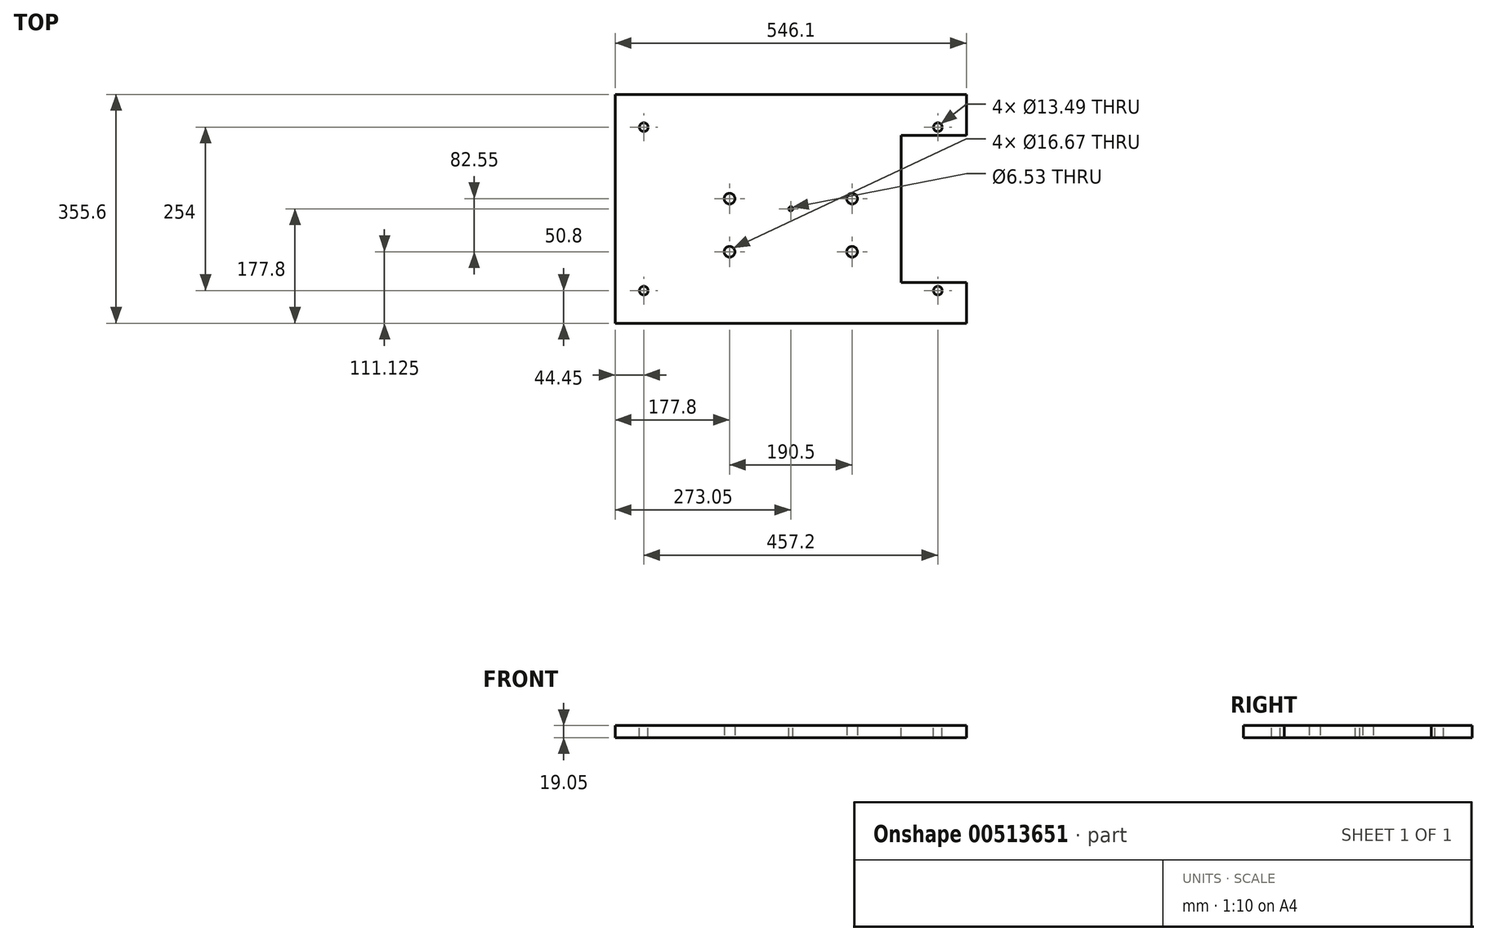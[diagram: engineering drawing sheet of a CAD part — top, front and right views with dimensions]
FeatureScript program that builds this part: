
annotation { "Feature Type Name" : "Feature", "Feature Type Description" : "" }
export const myFeature = defineFeature(function(context is Context, id is Id, definition is map)
    precondition{}
    {
        {
            var Q0;
            Q0=qCreatedBy(makeId("Top.planeOp"),FACE);
            var sketch = newSketch(context, id + "F0", { "sketchPlane" : qUnion([Q0])});
            skLineSegment(sketch, "E0.bottom", {"start": v(0, 0) * mm, "end": v(-546.1, 0) * mm});
            skLineSegment(sketch, "E0.top", {"start": v(0, 355.6) * mm, "end": v(-546.1, 355.6) * mm});
            skLineSegment(sketch, "E0.left", {"start": v(0, 0) * mm, "end": v(0, 355.6) * mm});
            skLineSegment(sketch, "E0.right", {"start": v(-546.1, 0) * mm, "end": v(-546.1, 355.6) * mm});
            skPoint(sketch, "E1", {"position": v(-501.65, 304.8) * mm});
            skPoint(sketch, "E2", {"position": v(-44.45, 304.8) * mm});
            skPoint(sketch, "E3", {"position": v(-44.45, 50.8) * mm});
            skPoint(sketch, "E4", {"position": v(-501.65, 50.8) * mm});
            skSolve(sketch);
        }
        {
            var Q0;
            Q0 = qSketchRegion(id + "F0", true);
            extrude(context, id + "F1", {"entities" : qUnion([Q0]), "depth" : 19.05 * mm});
        }
        {
            var Q0;
            Q0=makeQuery(id+"F1.opExtrude","CAP_FACE",FACE,{"disambiguationData":[OSD([sQuery(id+"F0.wireOp",EDGE,"E0.bottom"),sQuery(id+"F0.wireOp",EDGE,"E0.top"),sQuery(id+"F0.wireOp",EDGE,"E0.left"),sQuery(id+"F0.wireOp",EDGE,"E0.right")])],"isStart":false});
            var sketch = newSketch(context, id + "F2", { "sketchPlane" : qUnion([Q0])});
            skPoint(sketch, "E5", {"position": v(-501.65, 304.8) * mm});
            skPoint(sketch, "E6", {"position": v(-44.45, 304.8) * mm});
            skPoint(sketch, "E7", {"position": v(-44.45, 50.8) * mm});
            skPoint(sketch, "E8", {"position": v(-501.65, 50.8) * mm});
            skSolve(sketch);
        }
        {
            var Q0;
            Q0=sQuery(id+"F2.wireOp",VERTEX,"E5");
            var Q1;
            Q1=sQuery(id+"F2.wireOp",VERTEX,"E6");
            var Q2;
            Q2=sQuery(id+"F2.wireOp",VERTEX,"E7");
            var Q3;
            Q3=sQuery(id+"F2.wireOp",VERTEX,"E8");
            var Q4;
            Q4=makeQuery(id+"F1.opExtrude","SWEPT_BODY",BODY,{"disambiguationData":[OSD([sQuery(id+"F0.wireOp",EDGE,"E0.bottom"),sQuery(id+"F0.wireOp",EDGE,"E0.top"),sQuery(id+"F0.wireOp",EDGE,"E0.left"),sQuery(id+"F0.wireOp",EDGE,"E0.right")])]});
            hole(context, id + "F3", {"style" : HoleStyle.SIMPLE, "endStyle" : HoleEndStyle.THROUGH, "standardTappedOrClearance" : lookupTablePath({ "standard" : "ANSI", "fit" : "Normal (ASME)", "size" : "1/2", "type" : "Clearance" }), "standardBlindInLast" : lookupTablePath({ "fit" : "Free", "standard" : "ANSI", "size" : "1/2", "type" : "Clearance" }), "holeDiameter" : 13.5 * mm, "isTappedThrough" : true, "tappedDepth" : 8.9 * mm, "tapClearance" : 1, "locations" : qUnion([Q0, Q1, Q2, Q3]), "scope" : qUnion([Q4])});
        }
        {
            var Q0;
            Q0=makeQuery(id+"F1.opExtrude","CAP_FACE",FACE,{"disambiguationData":[OSD([sQuery(id+"F0.wireOp",EDGE,"E0.bottom"),sQuery(id+"F0.wireOp",EDGE,"E0.top"),sQuery(id+"F0.wireOp",EDGE,"E0.left"),sQuery(id+"F0.wireOp",EDGE,"E0.right")])],"isStart":false});
            var sketch = newSketch(context, id + "F4", { "sketchPlane" : qUnion([Q0])});
            skLineSegment(sketch, "E9.bottom", {"start": v(0, 292.1) * mm, "end": v(-101.6, 292.1) * mm});
            skLineSegment(sketch, "E9.top", {"start": v(0, 63.5) * mm, "end": v(-101.6, 63.5) * mm});
            skLineSegment(sketch, "E9.left", {"start": v(0, 292.1) * mm, "end": v(0, 63.5) * mm});
            skLineSegment(sketch, "E9.right", {"start": v(-101.6, 292.1) * mm, "end": v(-101.6, 63.5) * mm});
            skSolve(sketch);
        }
        {
            var Q0;
            Q0 = qSketchRegion(id + "F4", true);
            extrude(context, id + "F5", {"entities" : qUnion([Q0]), "operationType" : NewBodyOperationType.REMOVE, "oppositeDirection" : true, "depth" : 19.05 * mm});
        }
        {
            var Q0;
            Q0=makeQuery(id+"F1.opExtrude","CAP_FACE",FACE,{"disambiguationData":[OSD([sQuery(id+"F0.wireOp",EDGE,"E0.bottom"),sQuery(id+"F0.wireOp",EDGE,"E0.top"),sQuery(id+"F0.wireOp",EDGE,"E0.left"),sQuery(id+"F0.wireOp",EDGE,"E0.right")])],"isStart":false});
            var sketch = newSketch(context, id + "F6", { "sketchPlane" : qUnion([Q0])});
            skPoint(sketch, "E10", {"position": v(-330.2, 234.95) * mm});
            skPoint(sketch, "E11", {"position": v(-215.9, 234.95) * mm});
            skPoint(sketch, "E12", {"position": v(-215.9, 120.65) * mm});
            skPoint(sketch, "E13", {"position": v(-330.2, 120.65) * mm});
            skSolve(sketch);
        }
        {
            var Q0;
            Q0=makeQuery(id+"F1.opExtrude","CAP_FACE",FACE,{"disambiguationData":[OSD([sQuery(id+"F0.wireOp",EDGE,"E0.bottom"),sQuery(id+"F0.wireOp",EDGE,"E0.top"),sQuery(id+"F0.wireOp",EDGE,"E0.left"),sQuery(id+"F0.wireOp",EDGE,"E0.right")])],"isStart":false});
            var sketch = newSketch(context, id + "F7", { "sketchPlane" : qUnion([Q0])});
            skPoint(sketch, "E14", {"position": v(-273.05, 177.8) * mm});
            skSolve(sketch);
        }
        {
            var Q0;
            Q0=sQuery(id+"F7.wireOp",VERTEX,"E14");
            var Q1;
            Q1=makeQuery(id+"F1.opExtrude","SWEPT_BODY",BODY,{"disambiguationData":[OSD([sQuery(id+"F0.wireOp",EDGE,"E0.bottom"),sQuery(id+"F0.wireOp",EDGE,"E0.top"),sQuery(id+"F0.wireOp",EDGE,"E0.left"),sQuery(id+"F0.wireOp",EDGE,"E0.right")])]});
            hole(context, id + "F8", {"style" : HoleStyle.SIMPLE, "endStyle" : HoleEndStyle.THROUGH, "standardTappedOrClearance" : lookupTablePath({ "standard" : "ANSI", "fit" : "Close", "size" : "1/4", "type" : "Clearance" }), "standardBlindInLast" : lookupTablePath({ "fit" : "Close", "standard" : "ANSI", "size" : "1/4", "type" : "Clearance" }), "holeDiameter" : 6.53 * mm, "isTappedThrough" : true, "tappedDepth" : 8.9 * mm, "tapClearance" : 1, "locations" : qUnion([Q0]), "scope" : qUnion([Q1])});
        }
        {
            var Q0;
            Q0=makeQuery(id+"F0.imprint","IMPRINT",FACE,{"disambiguationData":[TD([[makeQuery(id+"F0.imprint","IMPRINT",EDGE,{"derivedFrom":sQuery(id+"F0.wireOp",EDGE,"E0.bottom")}),-1.0]])]});
            var sketch = newSketch(context, id + "F9", { "sketchPlane" : qUnion([Q0])});
            skPoint(sketch, "E15", {"position": v(-177.8, 193.67) * mm});
            skPoint(sketch, "E16", {"position": v(-368.3, 193.67) * mm});
            skPoint(sketch, "E17", {"position": v(-368.3, 111.12) * mm});
            skPoint(sketch, "E18", {"position": v(-177.8, 111.12) * mm});
            skSolve(sketch);
        }
        {
            var Q0;
            Q0=sQuery(id+"F9.wireOp",VERTEX,"E15");
            var Q1;
            Q1=sQuery(id+"F9.wireOp",VERTEX,"E16");
            var Q2;
            Q2=sQuery(id+"F9.wireOp",VERTEX,"E17");
            var Q3;
            Q3=sQuery(id+"F9.wireOp",VERTEX,"E18");
            var Q4;
            Q4=makeQuery(id+"F1.opExtrude","SWEPT_BODY",BODY,{"disambiguationData":[OSD([sQuery(id+"F0.wireOp",EDGE,"E0.bottom"),sQuery(id+"F0.wireOp",EDGE,"E0.top"),sQuery(id+"F0.wireOp",EDGE,"E0.left"),sQuery(id+"F0.wireOp",EDGE,"E0.right")])]});
            hole(context, id + "F10", {"style" : HoleStyle.SIMPLE, "endStyle" : HoleEndStyle.THROUGH, "oppositeDirection" : true, "holeDiameter" : 16.67 * mm, "isTappedThrough" : true, "tappedDepth" : 8.9 * mm, "tapClearance" : 1, "locations" : qUnion([Q0, Q1, Q2, Q3]), "scope" : qUnion([Q4])});
        }
    });
